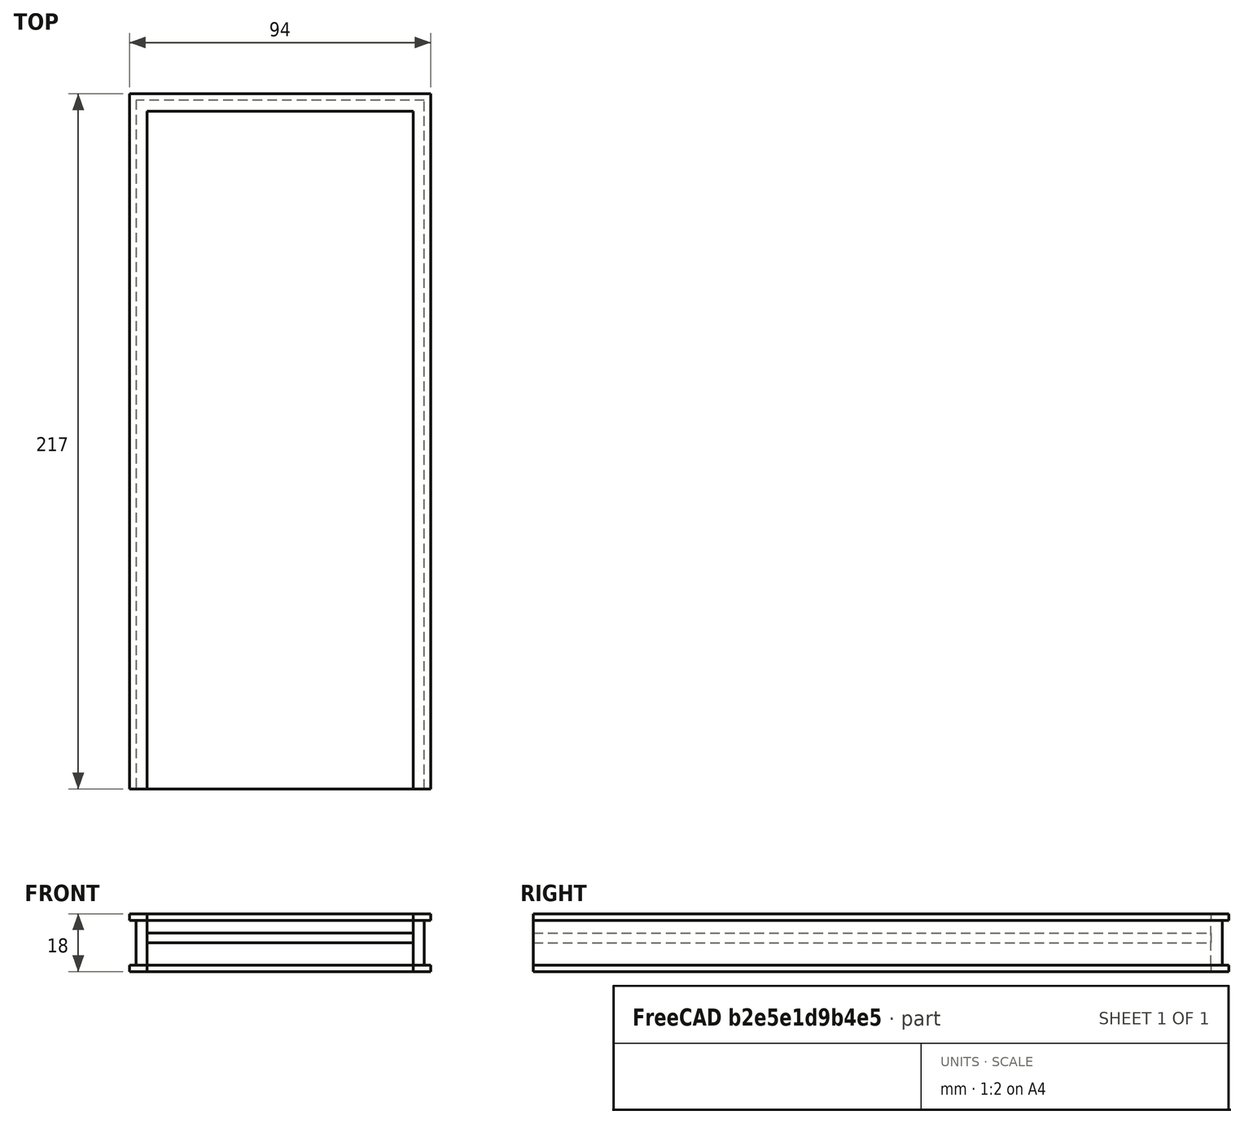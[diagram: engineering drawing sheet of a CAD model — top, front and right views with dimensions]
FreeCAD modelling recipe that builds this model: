
FCSTD DOCUMENT
Label: Simple door
License: CC-BY 3.0
LicenseURL: http://creativecommons.org/licenses/by/3.0/
objects: Sketcher::SketchObject×1, Part::FeaturePython×1
note: 2 computed .brp shape members not serialized (recipe doc carries the construction recipe); baked Part::Feature solids carry a one-line shape summary decoded from their .brp

FEATURE [Sketcher::SketchObject] Sketch
  sketch-geometry (12):
    g0: LineSegment StartX=0 StartY=0 StartZ=0 EndX=90 EndY=0 EndZ=0
    g1: LineSegment StartX=90 StartY=0 StartZ=0 EndX=90 EndY=215 EndZ=0
    g2: LineSegment StartX=90 StartY=215 StartZ=0 EndX=0 EndY=215 EndZ=0
    g3: LineSegment StartX=0 StartY=215 StartZ=0 EndX=0 EndY=0 EndZ=0
    g4: LineSegment StartX=3.5 StartY=0 StartZ=0 EndX=86.5 EndY=0 EndZ=0
    g5: LineSegment StartX=86.5 StartY=0 StartZ=0 EndX=86.5 EndY=211.5 EndZ=0
    g6: LineSegment StartX=86.5 StartY=211.5 StartZ=0 EndX=3.5 EndY=211.5 EndZ=0
    g7: LineSegment StartX=3.5 StartY=211.5 StartZ=0 EndX=3.5 EndY=0 EndZ=0
    g8: LineSegment StartX=-2 StartY=0 StartZ=0 EndX=92 EndY=0 EndZ=0
    g9: LineSegment StartX=92 StartY=0 StartZ=0 EndX=92 EndY=217 EndZ=0
    g10: LineSegment StartX=92 StartY=217 StartZ=0 EndX=-2 EndY=217 EndZ=0
    g11: LineSegment StartX=-2 StartY=217 StartZ=0 EndX=-2 EndY=0 EndZ=0
  constraints (36):
    c: Coincident(g0,g1)
    c: Coincident(g1,g2)
    c: Coincident(g2,g3)
    c: Coincident(g3,g0)
    c: Horizontal(g0)
    c: Horizontal(g2)
    c: Vertical(g1)
    c: Vertical(g3)
    c: DistanceX(g0) = 0
    c: DistanceY(g0) = 0
    c: DistanceX(g0) = 90
    c: DistanceY(g1) = 215
    c: Coincident(g4,g5)
    c: Coincident(g5,g6)
    c: Coincident(g6,g7)
    c: Coincident(g7,g4)
    c: Horizontal(g4)
    c: Horizontal(g6)
    c: Vertical(g5)
    c: Vertical(g7)
    c: DistanceY(g6,g2) = 3.5
    c: DistanceX(g6,g2) = -3.5
    c: DistanceX(g5,g1) = 3.5
    c: DistanceY(g4,g0) = 0
    c: Coincident(g8,g9)
    c: Coincident(g9,g10)
    c: Coincident(g10,g11)
    c: Coincident(g11,g8)
    c: Horizontal(g8)
    c: Horizontal(g10)
    c: Vertical(g9)
    c: Vertical(g11)
    c: DistanceX(g2,g10) = -2
    c: DistanceX(g1,g9) = 2
    c: DistanceY(g2,g10) = 2
    c: DistanceY(g8,g0) = 0
FEATURE [Part::FeaturePython] Window  # WARN: FeaturePython — macro-defined, semantics opaque (R4)
  Base = -> Sketch
  WindowParts = Main frame | Frame | Wire0,Wire1 | -14 | 0 | Door sheet | Solid panel | Wire1 | 3 | -10 | Front finish | Frame | Wire1,Wire2 | 2 | -16 | Rear finish | Frame | Wire1,Wire2 | 2 | 0
